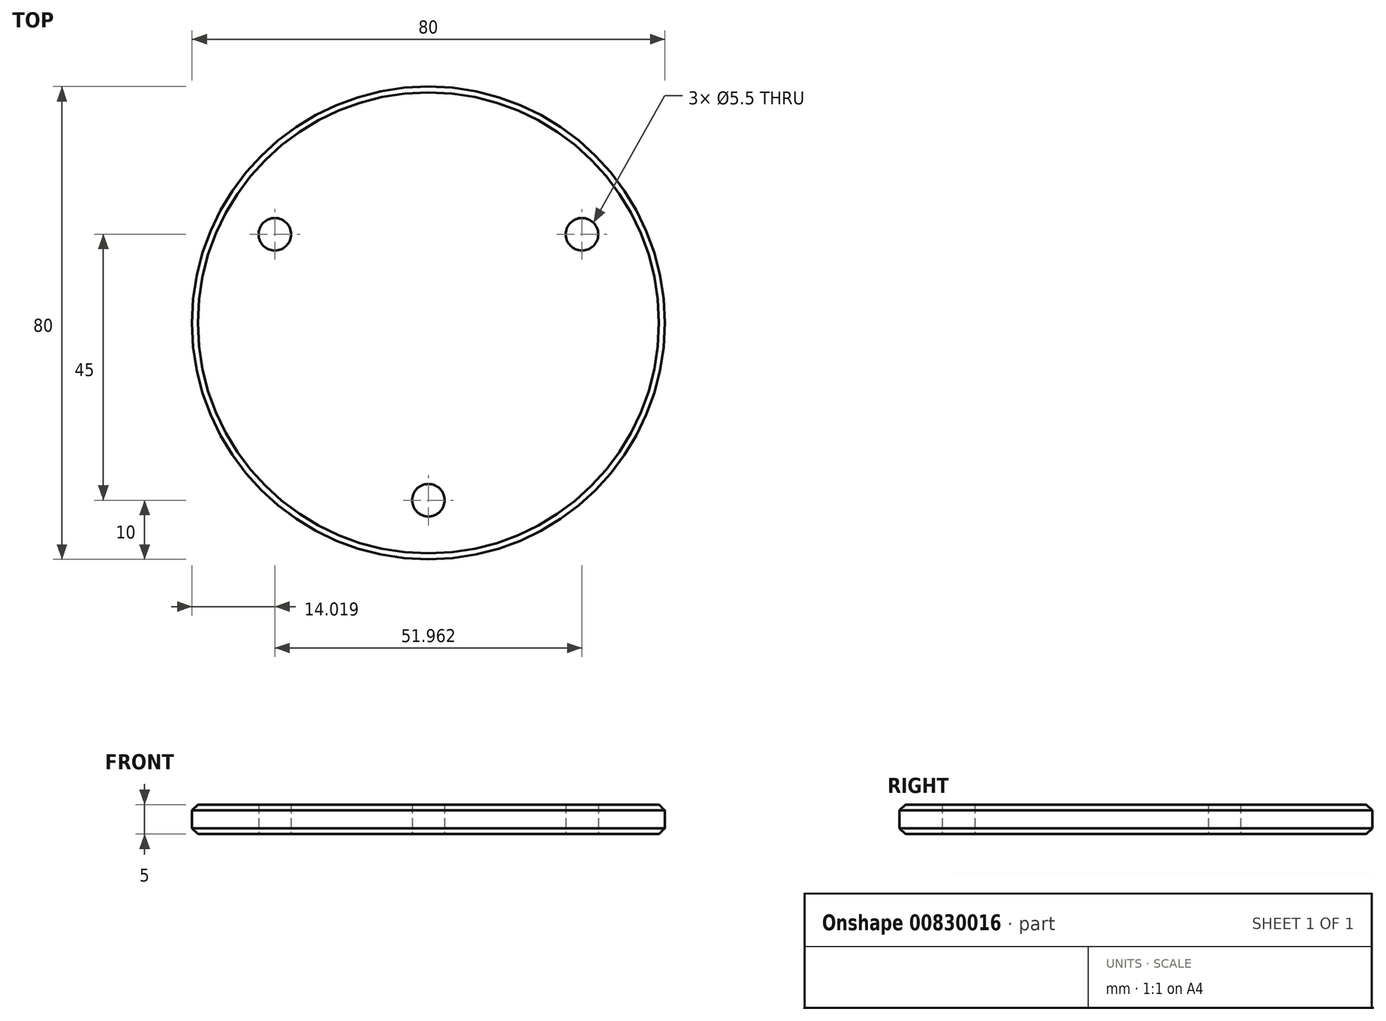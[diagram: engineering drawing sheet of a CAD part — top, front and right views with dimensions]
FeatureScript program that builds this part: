
annotation { "Feature Type Name" : "Feature", "Feature Type Description" : "" }
export const myFeature = defineFeature(function(context is Context, id is Id, definition is map)
    precondition{}
    {
        {
            var Q0;
            Q0=qCreatedBy(makeId("Top.planeOp"),FACE);
            var sketch = newSketch(context, id + "F0", { "sketchPlane" : qUnion([Q0])});
            skCircle(sketch, "E0", {"center": v(0, 0) * mm, "radius": 40 * mm});
            skSolve(sketch);
        }
        {
            var Q0;
            Q0=makeQuery(id+"F0.imprint","IMPRINT",FACE,{"disambiguationData":[TD([[makeQuery(id+"F0.imprint","IMPRINT",EDGE,{"derivedFrom":sQuery(id+"F0.wireOp",EDGE,"E0")}),1.0]])]});
            extrude(context, id + "F1", {"entities" : qUnion([Q0]), "depth" : 5 * mm, "offsetDistance" : 25 * mm});
        }
        {
            var Q0;
            Q0=makeQuery(id+"F1.opExtrude","CAP_FACE",FACE,{"disambiguationData":[OSD([sQuery(id+"F0.wireOp",EDGE,"E0")])],"isStart":true});
            var sketch = newSketch(context, id + "F2", { "sketchPlane" : qUnion([Q0])});
            skCircle(sketch, "E1", {"center": v(0, 0) * mm, "radius": 30 * mm, "construction": true});
            skPoint(sketch, "E2", {"position": v(0, 30) * mm});
            skLineSegment(sketch, "E3", {"start": v(0, 0) * mm, "end": v(0, 30) * mm, "construction": true});
            skLineSegment(sketch, "E4", {"start": v(0, 0) * mm, "end": v(25.98, -15) * mm, "construction": true});
            skLineSegment(sketch, "E5", {"start": v(-25.98, -15) * mm, "end": v(0, 0) * mm, "construction": true});
            skSolve(sketch);
        }
        {
            var Q0;
            Q0=sQuery(id+"F2.wireOp",VERTEX,"E2");
            var Q1;
            Q1=sQuery(id+"F2.wireOp",VERTEX,"E4.end");
            var Q2;
            Q2=sQuery(id+"F2.wireOp",VERTEX,"E5.start");
            var Q3;
            Q3=makeQuery(id+"F1.opExtrude","SWEPT_BODY",BODY,{"disambiguationData":[OSD([sQuery(id+"F0.wireOp",EDGE,"E0")])]});
            hole(context, id + "F3", {"style" : HoleStyle.SIMPLE, "endStyle" : HoleEndStyle.THROUGH, "holeDiameter" : 5.5 * mm, "majorDiameter" : 5 * mm, "isTappedThrough" : true, "tappedDepth" : 12 * mm, "tapClearance" : 3, "locations" : qUnion([Q0, Q1, Q2]), "scope" : qUnion([Q3])});
        }
        {
            var Q0;
            Q0=makeQuery(id+"F1.opExtrude","CAP_EDGE",EDGE,{"disambiguationData":[OSD([sQuery(id+"F0.wireOp",EDGE,"E0")])],"isStart":false});
            var Q1;
            Q1=makeQuery(id+"F1.opExtrude","CAP_EDGE",EDGE,{"disambiguationData":[OSD([sQuery(id+"F0.wireOp",EDGE,"E0")])],"isStart":true});
            chamfer(context, id + "F4", {"entities" : qUnion([Q0, Q1]), "width" : 1 * mm, "tangentPropagation" : true});
        }
    });
